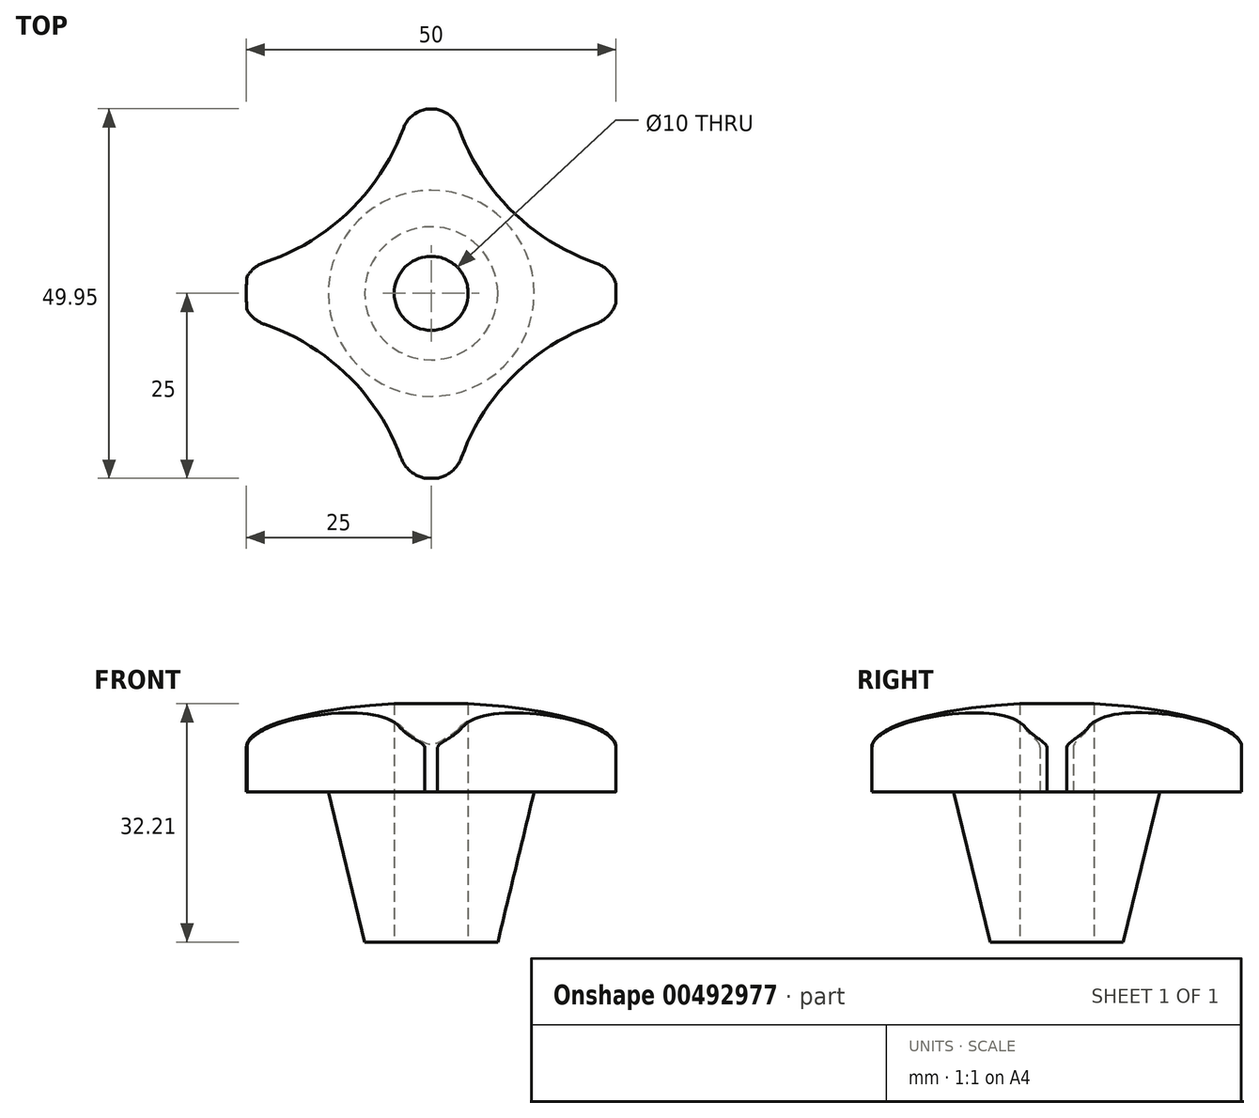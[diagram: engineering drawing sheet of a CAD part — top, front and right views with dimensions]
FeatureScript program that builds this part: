
annotation { "Feature Type Name" : "Feature", "Feature Type Description" : "" }
export const myFeature = defineFeature(function(context is Context, id is Id, definition is map)
    precondition{}
    {
        {
            var Q0;
            Q0=qCreatedBy(makeId("Right.planeOp"),FACE);
            var sketch = newSketch(context, id + "F0", { "sketchPlane" : qUnion([Q0])});
            skLineSegment(sketch, "E0", {"start": v(0, 0) * mm, "end": v(9, 0) * mm});
            skLineSegment(sketch, "E1", {"start": v(9, 0) * mm, "end": v(13.93, 20.33) * mm});
            skLineSegment(sketch, "E2", {"start": v(13.93, 20.33) * mm, "end": v(25, 20.33) * mm});
            skLineSegment(sketch, "E3", {"start": v(25, 26.33) * mm, "end": v(25, 20.33) * mm});
            skLineSegment(sketch, "E4", {"start": v(25, 20.33) * mm, "end": v(13.93, 20.33) * mm});
            skEllipticalArc(sketch, "E5", {});
            skLineSegment(sketch, "E6", {"start": v(0, 32.33) * mm, "end": v(0, 0) * mm});
            skLineSegment(sketch, "E7", {"start": v(25, 20.33) * mm, "end": v(25, 26.33) * mm});
            const initialGuessF0  = {"E5": [0, 0.026326649770140646, 1, 0, 0.025, 0.006, 0, 1.5707963267948966]};
            skSetInitialGuess(sketch, initialGuessF0);
            skSolve(sketch);
        }
        {
            var Q0;
            Q0=makeQuery(id+"F0.imprint","IMPRINT",FACE,{"disambiguationData":[TD([[makeQuery(id+"F0.imprint","IMPRINT",EDGE,{"derivedFrom":sQuery(id+"F0.wireOp",EDGE,"E0")}),1.0]])]});
            var Q1;
            Q1=sQuery(id+"F0.wireOp",EDGE,"E6");
            revolve(context, id + "F1", {"entities" : qUnion([Q0]), "axis" : qUnion([Q1]), "revolveType" : RevolveType.FULL});
        }
        {
            var Q0;
            Q0=qCreatedBy(makeId("Top.planeOp"),FACE);
            var sketch = newSketch(context, id + "F2", { "sketchPlane" : qUnion([Q0])});
            skArc(sketch, "E8", {"start": v(-22.47, 4.21) * mm, "mid": v(-25.5, 0.02) * mm, "end": v(-22.51, -4.2) * mm});
            skArc(sketch, "E9", {"start": v(-4.1, -22.22) * mm, "mid": v(0.01, -25.07) * mm, "end": v(4.1, -22.19) * mm});
            skArc(sketch, "E10", {"start": v(3.76, 22.3) * mm, "mid": v(0.01, 24.95) * mm, "end": v(-3.75, 22.33) * mm});
            skArc(sketch, "E11", {"start": v(22.29, -4.1) * mm, "mid": v(25.18, 0.02) * mm, "end": v(22.24, 4.1) * mm});
            skArc(sketch, "E12", {"start": v(3.76, 22.3) * mm, "mid": v(10.93, 11.1) * mm, "end": v(22.24, 4.1) * mm});
            skArc(sketch, "E13", {"start": v(22.29, -4.1) * mm, "mid": v(11.16, -11.1) * mm, "end": v(4.1, -22.19) * mm});
            skArc(sketch, "E14", {"start": v(-4.1, -22.22) * mm, "mid": v(-11.27, -11.13) * mm, "end": v(-22.51, -4.2) * mm});
            skArc(sketch, "E15", {"start": v(-22.47, 4.21) * mm, "mid": v(-11.04, 11.13) * mm, "end": v(-3.75, 22.33) * mm});
            skSolve(sketch);
        }
        {
            var Q0;
            Q0 = qSketchRegion(id + "F2", true);
            extrude(context, id + "F3", {"entities" : qUnion([Q0]), "operationType" : NewBodyOperationType.INTERSECT, "depth" : 100 * mm});
        }
        {
            var Q0;
            Q0=makeQuery(id+"F1.opRevolve","SWEPT_FACE",FACE,{"disambiguationData":[OSD([sQuery(id+"F0.wireOp",EDGE,"E0")])]});
            var sketch = newSketch(context, id + "F4", { "sketchPlane" : qUnion([Q0])});
            skPoint(sketch, "E16", {"position": v(0, 0) * mm});
            skSolve(sketch);
        }
        {
            var Q0;
            Q0=sQuery(id+"F4.wireOp",VERTEX,"E16");
            var Q1;
            Q1=makeQuery(id+"F1.opRevolve","SWEPT_BODY",BODY,{"disambiguationData":[OSD([sQuery(id+"F0.wireOp",EDGE,"E0"),sQuery(id+"F0.wireOp",EDGE,"E4"),sQuery(id+"F0.wireOp",EDGE,"E5"),sQuery(id+"F0.wireOp",EDGE,"E6"),sQuery(id+"F0.wireOp",EDGE,"E1"),sQuery(id+"F0.wireOp",EDGE,"E7")])]});
            hole(context, id + "F5", {"style" : HoleStyle.SIMPLE, "endStyle" : HoleEndStyle.THROUGH, "holeDiameter" : 10 * mm, "isTappedThrough" : true, "tappedDepth" : 12 * mm, "tapClearance" : 3, "locations" : qUnion([Q0]), "scope" : qUnion([Q1])});
        }
    });
